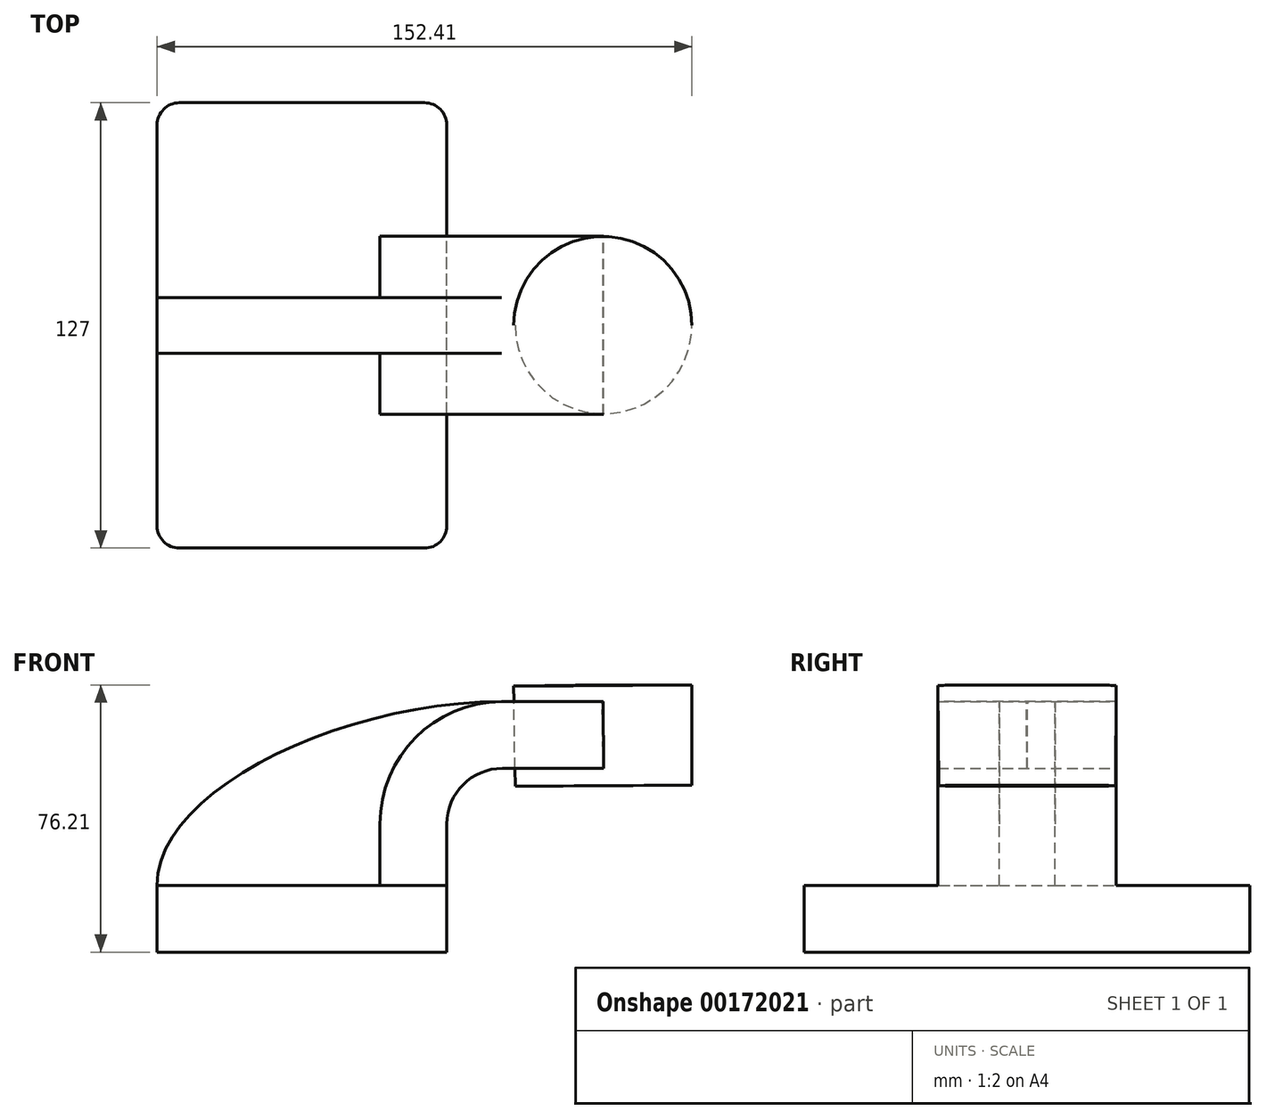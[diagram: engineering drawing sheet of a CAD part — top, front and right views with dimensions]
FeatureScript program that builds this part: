
annotation { "Feature Type Name" : "Feature", "Feature Type Description" : "" }
export const myFeature = defineFeature(function(context is Context, id is Id, definition is map)
    precondition{}
    {
        {
            var Q0;
            Q0=qCreatedBy(makeId("Front.planeOp"),FACE);
            var sketch = newSketch(context, id + "F0", { "sketchPlane" : qUnion([Q0])});
            skLineSegment(sketch, "E0.bottom", {"start": v(41.28, -9.52) * mm, "end": v(-41.27, -9.52) * mm});
            skLineSegment(sketch, "E0.top", {"start": v(41.27, 9.53) * mm, "end": v(-41.27, 9.53) * mm});
            skLineSegment(sketch, "E0.left", {"start": v(41.28, -9.52) * mm, "end": v(41.28, 9.53) * mm});
            skLineSegment(sketch, "E0.right", {"start": v(-41.27, -9.52) * mm, "end": v(-41.27, 9.53) * mm});
            skPoint(sketch, "E0.middle", {"position": v(0, 0) * mm});
            skLineSegment(sketch, "E1.bottom", {"start": v(111.12, 38.1) * mm, "end": v(60.33, 38.1) * mm});
            skLineSegment(sketch, "E1.top", {"start": v(111.12, 66.68) * mm, "end": v(60.33, 66.68) * mm});
            skLineSegment(sketch, "E1.left", {"start": v(111.12, 38.1) * mm, "end": v(111.12, 66.68) * mm});
            skLineSegment(sketch, "E1.right", {"start": v(60.33, 38.1) * mm, "end": v(60.33, 66.68) * mm});
            skPoint(sketch, "E1.middle", {"position": v(85.72, 52.39) * mm});
            skLineSegment(sketch, "E2", {"start": v(41.27, 9.53) * mm, "end": v(41.27, 27) * mm});
            skArc(sketch, "E3", {"start": v(41.27, 27) * mm, "mid": v(45.92, 38.23) * mm, "end": v(57.15, 42.88) * mm});
            skLineSegment(sketch, "E4", {"start": v(57.15, 42.88) * mm, "end": v(85.93, 42.88) * mm});
            skLineSegment(sketch, "E5.0", {"start": v(57.15, 61.93) * mm, "end": v(85.93, 61.93) * mm});
            skArc(sketch, "E5.1", {"start": v(22.22, 27) * mm, "mid": v(32.45, 51.7) * mm, "end": v(57.15, 61.93) * mm});
            skLineSegment(sketch, "E5.2", {"start": v(22.22, 9.53) * mm, "end": v(22.22, 27) * mm});
            skLineSegment(sketch, "E6", {"start": v(85.93, 61.93) * mm, "end": v(85.93, 42.88) * mm});
            skLineSegment(sketch, "E7", {"start": v(85.72, 66.68) * mm, "end": v(85.93, 38.1) * mm});
            skFitSpline(sketch, "E8", {"points": [v(-41.27, 9.53) * mm, v(57.15, 61.93) * mm], "startDerivative": vector(-0.8, 80) * mm, "endDerivative": vector(140.86, 0.37) * mm});
            skSolve(sketch);
        }
        {
            var Q0;
            Q0=makeQuery(id+"F0.imprint","IMPRINT",FACE,{"disambiguationData":[TD([[makeQuery(id+"F0.imprint","IMPRINT",EDGE,{"derivedFrom":sQuery(id+"F0.wireOp",EDGE,"E0.bottom")}),-1.0]])]});
            extrude(context, id + "F1", {"entities" : qUnion([Q0]), "endBound" : BoundingType.SYMMETRIC, "depth" : 127 * mm});
        }
        {
            var Q0;
            {var subQ7=sQuery(id+"F0.wireOp",EDGE,"E2");Q0=makeQuery(id+"F0.imprint","IMPRINT",FACE,{"disambiguationData":[TD([[makeQuery(id+"F0.imprint","IMPRINT",EDGE,{"derivedFrom":subQ7}),1.0]])]});}
            var Q1;
            {var subQ0=sQuery(id+"F0.wireOp",EDGE,"E4");var subQ1=sQuery(id+"F0.wireOp",EDGE,"E1.right");var subQ2=makeQuery(id+"F0.imprint","INTERSECT",VERTEX,{"derivedFrom":[subQ1,subQ0]});Q1=makeQuery(id+"F0.imprint","IMPRINT",FACE,{"disambiguationData":[TD([[makeQuery(id+"F0.imprint","IMPRINT",EDGE,{"disambiguationData":[TD([[subQ2,-1.0]])],"derivedFrom":subQ1}),-1.0]])]});}
            extrude(context, id + "F2", {"entities" : qUnion([Q0, Q1]), "operationType" : NewBodyOperationType.ADD, "endBound" : BoundingType.SYMMETRIC, "depth" : 50.8 * mm});
        }
        {
            var Q0;
            {var subQ3=sQuery(id+"F0.wireOp",EDGE,"E5.2");Q0=makeQuery(id+"F0.imprint","IMPRINT",FACE,{"disambiguationData":[TD([[makeQuery(id+"F0.imprint","IMPRINT",EDGE,{"derivedFrom":subQ3}),1.0]])]});}
            extrude(context, id + "F3", {"entities" : qUnion([Q0]), "operationType" : NewBodyOperationType.ADD, "endBound" : BoundingType.SYMMETRIC, "depth" : 15.88 * mm});
        }
        {
            var Q0;
            {var subQ4=sQuery(id+"F0.wireOp",EDGE,"E1.left");Q0=makeQuery(id+"F0.imprint","IMPRINT",FACE,{"disambiguationData":[TD([[makeQuery(id+"F0.imprint","IMPRINT",EDGE,{"derivedFrom":subQ4}),1.0]])]});}
            var Q1;
            Q1=sQuery(id+"F0.wireOp",EDGE,"E1.left");
            var Q2;
            Q2=sQuery(id+"F0.wireOp",EDGE,"E7");
            revolve(context, id + "F4", {"entities" : qUnion([Q0]), "surfaceEntities" : qUnion([Q1]), "axis" : qUnion([Q2]), "revolveType" : RevolveType.FULL});
        }
        {
            var Q0;
            Q0=makeQuery(id+"F1.opExtrude","CAP_EDGE",EDGE,{"disambiguationData":[OSD([sQuery(id+"F0.wireOp",EDGE,"E0.left")])],"isStart":true});
            var Q1;
            Q1=makeQuery(id+"F1.opExtrude","CAP_EDGE",EDGE,{"disambiguationData":[OSD([sQuery(id+"F0.wireOp",EDGE,"E0.right")])],"isStart":true});
            var Q2;
            Q2=makeQuery(id+"F1.opExtrude","CAP_EDGE",EDGE,{"disambiguationData":[OSD([sQuery(id+"F0.wireOp",EDGE,"E0.right")])],"isStart":false});
            var Q3;
            Q3=makeQuery(id+"F1.opExtrude","CAP_EDGE",EDGE,{"disambiguationData":[OSD([sQuery(id+"F0.wireOp",EDGE,"E0.left")])],"isStart":false});
            fillet(context, id + "F5", {"entities" : qUnion([Q0, Q1, Q2, Q3]), "radius" : 6.35 * mm, "tangentPropagation" : true, "allowEdgeOverflow" : false});
        }
    });
